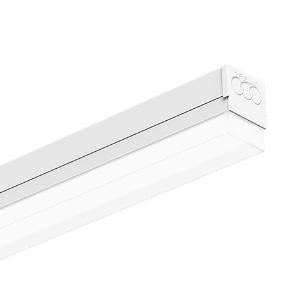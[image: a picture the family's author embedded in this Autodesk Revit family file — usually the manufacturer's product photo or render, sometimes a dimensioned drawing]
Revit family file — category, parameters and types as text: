
# Revit family: 3f_filippi_-_3f_zeta_dr_3f_filippi_-_10880_-_3f_zeta_dr_2x22_led_l1489
name_source: partatom
category: Lighting Fixtures
units: mm (PartAtom-declared; Revit-internal decimal feet)

## family parameters
Cut with Voids When Loaded = No
Host = Face
Light Source = No
Part Type = Normal
Room Calculation Point = No
Round Connector Dimension = Use Diameter
Shared = No

## types (1)
- 3F Filippi - 3F Zeta DR (1 x LED, 6253 lm, 49 W, 4000 K)
    Apparent Load = 49 VA
    Approval mark = CE
    CIE Flux Codes = 41 72 91 86 100
    Color Rendering = 80
    Color Temperature = 4000 K
    Control Gear = Electronic ballast
    Default Elevation = 1800 mm
    Description = ILLUMINOTECHNICAL
Luminous efficiency 100% (DLOR 86%, ULOR 14%).
Initial luminous flux of the luminaire 6253 lm.
Diffused symmetric distribution.
Installation Interdistance Transv.D = 1.31 x hu - Long.D = 1.25 x hu.
Tabular UGR (CIE 117 - 4H-8H; S=0.25H; 70/50/20): RUG 25.7 - 24.2.
Beam angle: 136° - 112°.
Luminous efficacy 128 lm/W.
Lifetime (L93/B10): 30000 h. (tq+25°C)
Lifetime (L90/B10): 50000 h. (tq+25°C)
Lifetime (L85/B10): 80000 h. (tq+25°C)
Lifetime (L80/B10): 100000 h. (tq+25°C)
Sudden decreased luminous flux after 50000 hours: 0% (C0).
Photobiological safety in compliance with IEC/TR 62778: RG0 risk exempt, (IEC 62471).
In compliance with IEC/EN 62722-2-1 - IEC/EN 62717 standards.

SOURCE
2 linear LED modules 22W/840.
Energy efficiency class (UE 2019/2020 - UE 2019/2015): D.
CIE 13.3 Colour rendering index: CRI >80 (R9 <50%).
IES TM-30 Fidelity Index: Rf = 84 Rg = 95.
CCT nominal colour temperature 4000 K.
Colour initial tolerance (MacAdam): SDCM 3.

MECHANICAL
Housing in hot-galvanised steel, painted in white polyester, obtained through rolling process.
Light unit in hot-galvanised steel, painted in white polyester base with fixing springs and retractable safety hooks in stainless steel.
Rectangular screen in self-extinguishing polycarbonate, UV stabilised, opal, with smooth outer surface.
End caps in white polycarbonate.
Pair of stainless steel sliding brackets with sliding block screws.
Luminaire with limited surface temperature. - D - (EN 60598-2-24)
Dimensions: 1489x62 mm, height 81 mm. Weight 3.47 kg.
IP40 protection degree.
Mechanical strength to impacts IK06 (1 joule).
Glow-wire test resistance 850°C.

ELECTRICAL
Halogen Free electronic wiring 230V-50/60Hz, power factor 0.95, THD <25%, constant output current, SELV, class I, 1 driver.
Power of the luminaire 49 W.
ENEC - CE.
SAFE FLICKER: PstLM=<1 and SVM=<0.4 (IEC TR 61547-1 and IEC TR 63158), to ensure a more comfortable and safe light.
Luminaire compliant with EN 60598-2-22 for power supply from a centralised emergency system CPSS (Central Power Supply System), not incorporated in the luminaire - high risk areas excluded. The default power and flux are 100% in AC and 100% in DC.
Ambient temperature from 0°C to +25°C.
Temperature class T6 max 85°C.
Relative humidity UR: <85%.

INSTALLATION
Ceiling / Suspended / Wall.
All accessories dedicated to this product are available on the Catalog and on our website www.3F-Filippi.com.

APPLICATIONS
Suitable product for food production plants (HACCP), IFS (Food Version 6), BRC (GSFS Food Version 7).
In commercial environments, exhibition areas, shops and stores.

WARNING
Luminaire designed for disposal/recycling at end-of-life.
Replaceable (LED only) light source by a professional. Replaceable control gear by a professional.
    Height = 81 mm
    Lamp = 1 x LED
    Lamp Light Flux = 6253 lm
    Lamp Power = 49 W
    Lamp count = 1
    Length = 1489 mm
    Lifetime = 50000 h
    Luminous efficacy = 128 lm/W
    Manufacturer = 3F Filippi
    ModVariant = No
    Model = 3F Filippi - 10880 - 3F Zeta DR 2x22 LED L1489
    Mounting Place = Ceiling
    Mounting Type = Pendant
    Number of Poles = 1
    OnlyDefault = Yes
    Power Factor = 1
    Product Name = 3F Filippi - 3F Zeta DR
    Product group = pendant luminaire
    ProductGroupID = 9
    Protection Class = Protection class I
    Protection Degree = IP 40
    RLX_Detail_Level = 1
    RLX_Emergency_Light_Flux = 0 lm
    RLX_Emergency_Type = 0
    RLX_Emergency_Type_DB = No
    RlxData = <blob elided: 32989 chars, md5=5aa6ecc2>
    Socket = socket
    Standby Power = 0 W
    System Light Flux = 6253 lm
    System Power = 49 W
    Type Comments = Product without accessories
    Type Image = 3ffilippi_3f_zeta_dr.jpg
    URL = http://relux.com
    VarID = ---
    Voltage = 0 V
    Weight = 0.00 kg
    Width = 62 mm  [stored 0.203412 ft]

note: [stored X ft] marks values corroborated as IEEE doubles in the binary element streams (Revit-internal decimal feet)

## geometry (parser evidence)
native form markers: Blend x4, Sweep x11
no freeform markers — native parametric forms only
